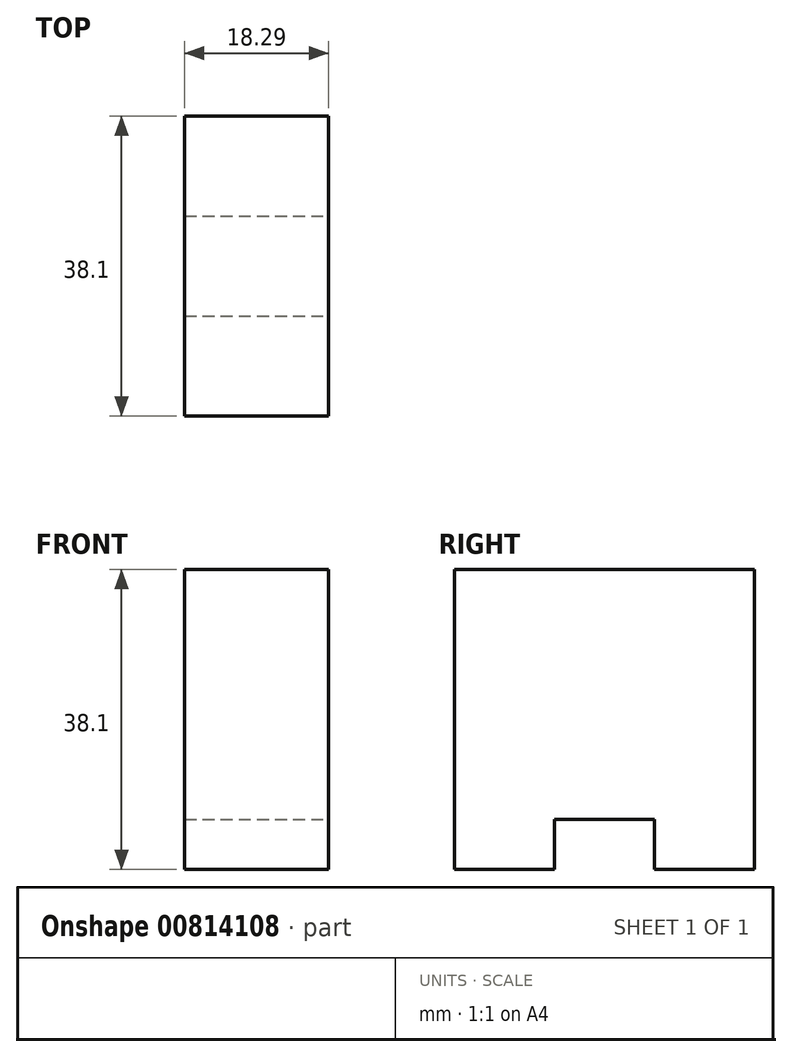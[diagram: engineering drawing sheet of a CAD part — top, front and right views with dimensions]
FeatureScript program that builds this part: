
annotation { "Feature Type Name" : "Feature", "Feature Type Description" : "" }
export const myFeature = defineFeature(function(context is Context, id is Id, definition is map)
    precondition{}
    {
        {
            var Q0;
            Q0=qCreatedBy(makeId("Right.planeOp"),FACE);
            var sketch = newSketch(context, id + "F0", { "sketchPlane" : qUnion([Q0])});
            skLineSegment(sketch, "E0", {"start": v(0, 0) * mm, "end": v(12.7, 0) * mm});
            skLineSegment(sketch, "E1", {"start": v(12.7, 0) * mm, "end": v(12.7, 6.35) * mm});
            skLineSegment(sketch, "E2", {"start": v(12.7, 6.35) * mm, "end": v(25.4, 6.35) * mm});
            skLineSegment(sketch, "E3", {"start": v(25.4, 6.35) * mm, "end": v(25.4, 0) * mm});
            skLineSegment(sketch, "E4", {"start": v(25.4, 0) * mm, "end": v(38.1, 0) * mm});
            skLineSegment(sketch, "E5", {"start": v(38.1, 0) * mm, "end": v(38.1, 38.1) * mm});
            skLineSegment(sketch, "E6", {"start": v(38.1, 38.1) * mm, "end": v(0, 38.1) * mm});
            skLineSegment(sketch, "E7", {"start": v(0, 38.1) * mm, "end": v(0, 0) * mm});
            skSolve(sketch);
        }
        {
            var Q0;
            Q0=makeQuery(id+"F0.imprint","IMPRINT",FACE,{"disambiguationData":[TD([[makeQuery(id+"F0.imprint","IMPRINT",EDGE,{"derivedFrom":sQuery(id+"F0.wireOp",EDGE,"E0")}),1.0]])]});
            extrude(context, id + "F1", {"entities" : qUnion([Q0]), "oppositeDirection" : true, "depth" : 18.29 * mm, "offsetDistance" : 25.4 * mm});
        }
    });
